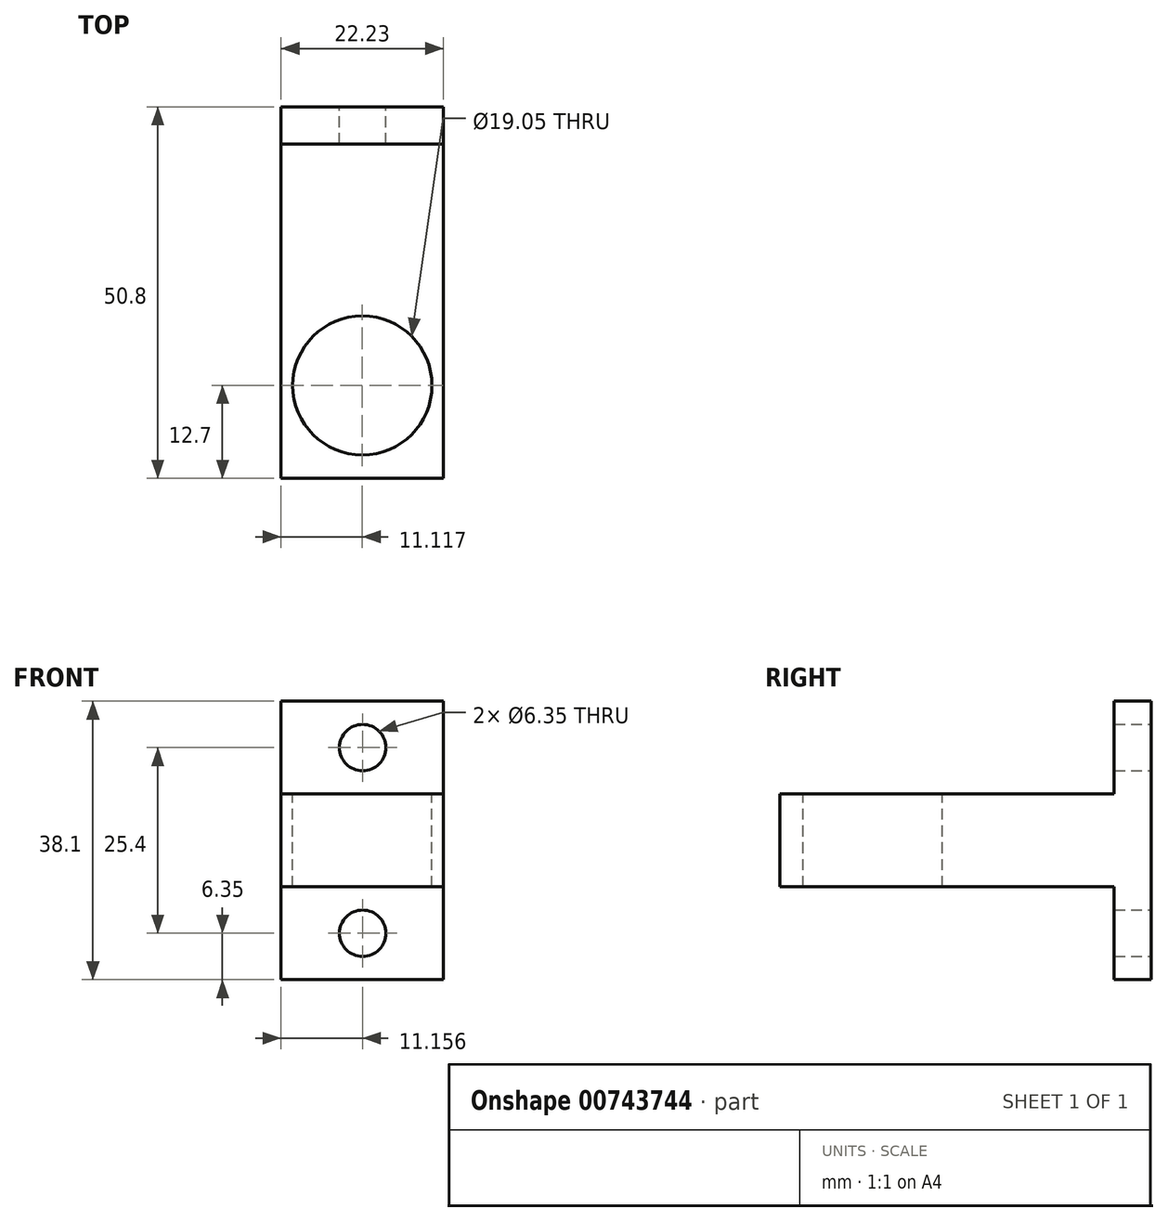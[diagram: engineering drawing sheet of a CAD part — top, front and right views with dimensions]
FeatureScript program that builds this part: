
annotation { "Feature Type Name" : "Feature", "Feature Type Description" : "" }
export const myFeature = defineFeature(function(context is Context, id is Id, definition is map)
    precondition{}
    {
        {
            var Q0;
            Q0=qCreatedBy(makeId("Front.planeOp"),FACE);
            var sketch = newSketch(context, id + "F0", { "sketchPlane" : qUnion([Q0])});
            skLineSegment(sketch, "E0", {"start": v(0, 0) * mm, "end": v(-22.23, 0) * mm});
            skLineSegment(sketch, "E1", {"start": v(-22.23, 0) * mm, "end": v(-22.23, 38.1) * mm});
            skLineSegment(sketch, "E2", {"start": v(-22.23, 38.1) * mm, "end": v(0, 38.1) * mm});
            skLineSegment(sketch, "E3", {"start": v(0, 38.1) * mm, "end": v(0, 0) * mm});
            skLineSegment(sketch, "E4", {"start": v(-22.23, 0) * mm, "end": v(-22.23, 12.7) * mm});
            skLineSegment(sketch, "E5", {"start": v(-22.23, 38.1) * mm, "end": v(-22.23, 25.4) * mm});
            skLineSegment(sketch, "E6", {"start": v(-22.23, 6.35) * mm, "end": v(-11.07, 6.35) * mm});
            skLineSegment(sketch, "E7", {"start": v(-22.23, 31.75) * mm, "end": v(-11.07, 31.75) * mm});
            skCircle(sketch, "E8", {"center": v(-11.07, 31.75) * mm, "radius": 3.18 * mm});
            skCircle(sketch, "E9", {"center": v(-11.07, 6.35) * mm, "radius": 3.18 * mm});
            skSolve(sketch);
        }
        {
            var Q0;
            Q0 = qSketchRegion(id + "F0", true);
            extrude(context, id + "F1", {"entities" : qUnion([Q0]), "depth" : 50.8 * mm, "offsetDistance" : 25.4 * mm});
        }
        {
            var Q0;
            Q0=makeQuery(id+"F1.opExtrude","CAP_FACE",FACE,{"disambiguationData":[OSD([sQuery(id+"F0.wireOp",EDGE,"E0"),sQuery(id+"F0.wireOp",EDGE,"E1"),sQuery(id+"F0.wireOp",EDGE,"E2"),sQuery(id+"F0.wireOp",EDGE,"E3"),sQuery(id+"F0.wireOp",EDGE,"E4"),sQuery(id+"F0.wireOp",EDGE,"E5"),sQuery(id+"F0.wireOp",EDGE,"E8"),sQuery(id+"F0.wireOp",EDGE,"E9")])],"isStart":false});
            var sketch = newSketch(context, id + "F2", { "sketchPlane" : qUnion([Q0])});
            skLineSegment(sketch, "E10", {"start": v(0, 38.1) * mm, "end": v(-22.23, 38.1) * mm});
            skLineSegment(sketch, "E11", {"start": v(-22.23, 38.1) * mm, "end": v(-22.23, 25.4) * mm});
            skLineSegment(sketch, "E12", {"start": v(-22.23, 25.4) * mm, "end": v(0, 25.4) * mm});
            skLineSegment(sketch, "E13", {"start": v(0, 0) * mm, "end": v(-22.23, 0) * mm});
            skLineSegment(sketch, "E14", {"start": v(-22.23, 0) * mm, "end": v(-22.23, 12.7) * mm});
            skLineSegment(sketch, "E15", {"start": v(-22.23, 12.7) * mm, "end": v(0, 12.7) * mm});
            skLineSegment(sketch, "E16", {"start": v(0, 12.7) * mm, "end": v(0, 0) * mm});
            skLineSegment(sketch, "E17", {"start": v(0, 38.1) * mm, "end": v(0, 25.4) * mm});
            skSolve(sketch);
        }
        {
            var Q0;
            Q0 = qSketchRegion(id + "F2", true);
            extrude(context, id + "F3", {"entities" : qUnion([Q0]), "operationType" : NewBodyOperationType.REMOVE, "oppositeDirection" : true, "depth" : 45.72 * mm, "offsetDistance" : 25.4 * mm});
        }
        {
            var Q0;
            Q0=makeQuery(id+"F3.boolean.opBoolean","COPY",FACE,{"derivedFrom":makeQuery(id+"F3.opExtrude","SWEPT_FACE",FACE,{"disambiguationData":[OSD([sQuery(id+"F2.wireOp",EDGE,"E12")])]})});
            var sketch = newSketch(context, id + "F4", { "sketchPlane" : qUnion([Q0])});
            skLineSegment(sketch, "E18", {"start": v(0, -50.8) * mm, "end": v(-11.11, -50.8) * mm});
            skLineSegment(sketch, "E19", {"start": v(-11.11, -50.8) * mm, "end": v(-11.11, -38.1) * mm});
            skCircle(sketch, "E20", {"center": v(-11.11, -38.1) * mm, "radius": 9.53 * mm});
            skSolve(sketch);
        }
        {
            var Q0;
            Q0 = qSketchRegion(id + "F4", true);
            extrude(context, id + "F5", {"entities" : qUnion([Q0]), "operationType" : NewBodyOperationType.REMOVE, "endBound" : BoundingType.THROUGH_ALL, "oppositeDirection" : true, "depth" : 25.4 * mm, "offsetDistance" : 25.4 * mm});
        }
    });
